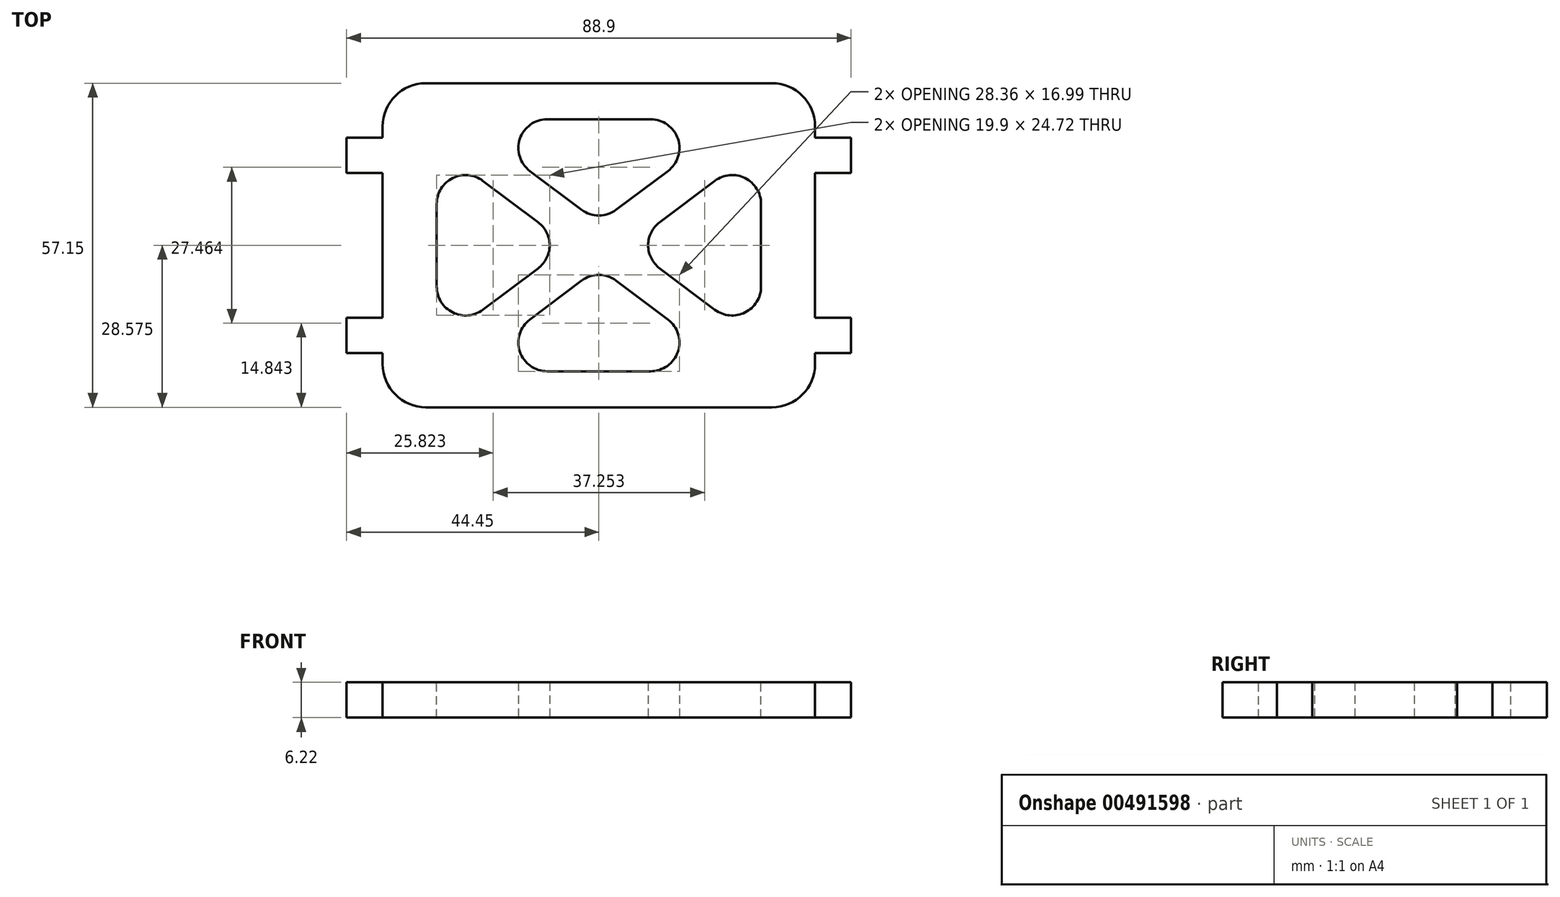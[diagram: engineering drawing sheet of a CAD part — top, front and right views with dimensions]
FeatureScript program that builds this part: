
annotation { "Feature Type Name" : "Feature", "Feature Type Description" : "" }
export const myFeature = defineFeature(function(context is Context, id is Id, definition is map)
    precondition{}
    {
        {
            var Q0;
            Q0=qCreatedBy(makeId("Top.planeOp"),FACE);
            var sketch = newSketch(context, id + "F0", { "sketchPlane" : qUnion([Q0])});
            skLineSegment(sketch, "E0", {"start": v(0, 0) * mm, "end": v(38.1, 0) * mm});
            skLineSegment(sketch, "E1", {"start": v(38.1, 57.15) * mm, "end": v(0, 57.15) * mm});
            skLineSegment(sketch, "E2", {"start": v(1.81, 12.7) * mm, "end": v(54.74, 12.7) * mm, "construction": true});
            skLineSegment(sketch, "E3", {"start": v(1.81, 44.45) * mm, "end": v(54.74, 44.45) * mm, "construction": true});
            skLineSegment(sketch, "E4", {"start": v(44.45, 44.45) * mm, "end": v(44.45, 47.56) * mm});
            skLineSegment(sketch, "E5", {"start": v(44.45, 47.56) * mm, "end": v(38.1, 47.56) * mm});
            skLineSegment(sketch, "E6", {"start": v(44.45, 44.45) * mm, "end": v(44.45, 41.34) * mm});
            skLineSegment(sketch, "E7", {"start": v(44.45, 41.34) * mm, "end": v(38.1, 41.34) * mm});
            skLineSegment(sketch, "E8", {"start": v(44.45, 12.7) * mm, "end": v(44.45, 15.81) * mm});
            skLineSegment(sketch, "E9", {"start": v(44.45, 15.81) * mm, "end": v(38.1, 15.81) * mm});
            skLineSegment(sketch, "E10", {"start": v(44.45, 12.7) * mm, "end": v(44.45, 9.59) * mm});
            skLineSegment(sketch, "E11", {"start": v(44.45, 9.59) * mm, "end": v(38.1, 9.59) * mm});
            skLineSegment(sketch, "E12", {"start": v(38.1, 9.59) * mm, "end": v(38.1, 0) * mm});
            skLineSegment(sketch, "E13", {"start": v(38.1, 15.81) * mm, "end": v(38.1, 41.34) * mm});
            skLineSegment(sketch, "E14", {"start": v(38.1, 47.56) * mm, "end": v(38.1, 57.15) * mm});
            skLineSegment(sketch, "E15.MirrorCS", {"start": v(-38.1, 57.15) * mm, "end": v(0, 57.15) * mm});
            skLineSegment(sketch, "E16.MirrorCS", {"start": v(-38.1, 47.56) * mm, "end": v(-38.1, 57.15) * mm});
            skLineSegment(sketch, "E17.MirrorCS", {"start": v(-44.45, 47.56) * mm, "end": v(-38.1, 47.56) * mm});
            skLineSegment(sketch, "E18.MirrorCS", {"start": v(-44.45, 44.45) * mm, "end": v(-44.45, 47.56) * mm});
            skLineSegment(sketch, "E19.MirrorCS", {"start": v(-44.45, 44.45) * mm, "end": v(-44.45, 41.34) * mm});
            skLineSegment(sketch, "E20.MirrorCS", {"start": v(-44.45, 41.34) * mm, "end": v(-38.1, 41.34) * mm});
            skLineSegment(sketch, "E21.MirrorCS", {"start": v(-38.1, 15.81) * mm, "end": v(-38.1, 41.34) * mm});
            skLineSegment(sketch, "E22.MirrorCS", {"start": v(-44.45, 15.81) * mm, "end": v(-38.1, 15.81) * mm});
            skLineSegment(sketch, "E23.MirrorCS", {"start": v(-44.45, 12.7) * mm, "end": v(-44.45, 15.81) * mm});
            skLineSegment(sketch, "E24.MirrorCS", {"start": v(-44.45, 12.7) * mm, "end": v(-44.45, 9.59) * mm});
            skLineSegment(sketch, "E25.MirrorCS", {"start": v(-44.45, 9.59) * mm, "end": v(-38.1, 9.59) * mm});
            skLineSegment(sketch, "E26.MirrorCS", {"start": v(-38.1, 9.59) * mm, "end": v(-38.1, 0) * mm});
            skLineSegment(sketch, "E27.MirrorCS", {"start": v(0, 0) * mm, "end": v(-38.1, 0) * mm});
            skSolve(sketch);
        }
        {
            var Q0;
            Q0 = qSketchRegion(id + "F0", true);
            extrude(context, id + "F1", {"entities" : qUnion([Q0]), "depth" : 6.22 * mm});
        }
        {
            var Q0;
            Q0=makeQuery(id+"F1.opExtrude","CAP_FACE",FACE,{"disambiguationData":[OSD([sQuery(id+"F0.wireOp",EDGE,"E0"),sQuery(id+"F0.wireOp",EDGE,"E1"),sQuery(id+"F0.wireOp",EDGE,"E4"),sQuery(id+"F0.wireOp",EDGE,"E5"),sQuery(id+"F0.wireOp",EDGE,"E6"),sQuery(id+"F0.wireOp",EDGE,"E7"),sQuery(id+"F0.wireOp",EDGE,"E8"),sQuery(id+"F0.wireOp",EDGE,"E9"),sQuery(id+"F0.wireOp",EDGE,"E10"),sQuery(id+"F0.wireOp",EDGE,"E11"),sQuery(id+"F0.wireOp",EDGE,"E12"),sQuery(id+"F0.wireOp",EDGE,"E13"),sQuery(id+"F0.wireOp",EDGE,"E14"),sQuery(id+"F0.wireOp",EDGE,"E15.MirrorCS"),sQuery(id+"F0.wireOp",EDGE,"E16.MirrorCS"),sQuery(id+"F0.wireOp",EDGE,"E17.MirrorCS"),sQuery(id+"F0.wireOp",EDGE,"E18.MirrorCS"),sQuery(id+"F0.wireOp",EDGE,"E19.MirrorCS"),sQuery(id+"F0.wireOp",EDGE,"E20.MirrorCS"),sQuery(id+"F0.wireOp",EDGE,"E21.MirrorCS"),sQuery(id+"F0.wireOp",EDGE,"E22.MirrorCS"),sQuery(id+"F0.wireOp",EDGE,"E23.MirrorCS"),sQuery(id+"F0.wireOp",EDGE,"E24.MirrorCS"),sQuery(id+"F0.wireOp",EDGE,"E25.MirrorCS"),sQuery(id+"F0.wireOp",EDGE,"E26.MirrorCS"),sQuery(id+"F0.wireOp",EDGE,"E27.MirrorCS")])],"isStart":false});
            var sketch = newSketch(context, id + "F2", { "sketchPlane" : qUnion([Q0])});
            skLineSegment(sketch, "E28", {"start": v(-38.1, 57.15) * mm, "end": v(38.1, 0) * mm, "construction": true});
            skLineSegment(sketch, "E29", {"start": v(38.1, 57.15) * mm, "end": v(-38.1, 0) * mm, "construction": true});
            skLineSegment(sketch, "E30", {"start": v(-31.75, -5.46) * mm, "end": v(-31.75, 61.03) * mm, "construction": true});
            skLineSegment(sketch, "E31", {"start": v(31.75, -6.6) * mm, "end": v(31.75, 61.6) * mm, "construction": true});
            skLineSegment(sketch, "E32", {"start": v(-44.69, 50.8) * mm, "end": v(46.98, 50.8) * mm, "construction": true});
            skLineSegment(sketch, "E33", {"start": v(-48, 6.35) * mm, "end": v(45.68, 6.35) * mm, "construction": true});
            skLineSegment(sketch, "E34", {"start": v(-28.57, 11.11) * mm, "end": v(-5.3, 28.58) * mm});
            skLineSegment(sketch, "E35", {"start": v(-5.3, 28.58) * mm, "end": v(-28.58, 46.04) * mm});
            skLineSegment(sketch, "E36", {"start": v(0, 32.54) * mm, "end": v(-24.34, 50.8) * mm});
            skLineSegment(sketch, "E37", {"start": v(-24.34, 50.8) * mm, "end": v(24.34, 50.8) * mm});
            skLineSegment(sketch, "E38", {"start": v(24.34, 50.8) * mm, "end": v(0, 32.54) * mm});
            skLineSegment(sketch, "E39", {"start": v(-28.58, 46.04) * mm, "end": v(-28.57, 11.11) * mm});
            skLineSegment(sketch, "E40.MirrorCS", {"start": v(5.3, 28.58) * mm, "end": v(28.58, 46.04) * mm});
            skLineSegment(sketch, "E41.MirrorCS", {"start": v(28.58, 46.04) * mm, "end": v(28.57, 11.11) * mm});
            skLineSegment(sketch, "E42.MirrorCS", {"start": v(28.57, 11.11) * mm, "end": v(5.3, 28.58) * mm});
            skLineSegment(sketch, "E43", {"start": v(-46.54, 28.57) * mm, "end": v(53.85, 28.57) * mm, "construction": true});
            skPoint(sketch, "E43.startSnap0", {"position": v(-38.1, 28.57) * mm});
            skLineSegment(sketch, "E44.MirrorCS", {"start": v(0, 24.6) * mm, "end": v(-24.34, 6.35) * mm});
            skLineSegment(sketch, "E45.MirrorCS", {"start": v(24.34, 6.35) * mm, "end": v(0, 24.6) * mm});
            skLineSegment(sketch, "E46.MirrorCS", {"start": v(-24.34, 6.35) * mm, "end": v(24.34, 6.35) * mm});
            skSolve(sketch);
        }
        {
            var Q0;
            Q0 = qSketchRegion(id + "F2", true);
            extrude(context, id + "F3", {"entities" : qUnion([Q0]), "operationType" : NewBodyOperationType.REMOVE, "oppositeDirection" : true, "depth" : 25.4 * mm});
        }
        {
            var Q0;
            Q0=makeQuery(id+"F3.boolean.opBoolean","COPY",EDGE,{"derivedFrom":makeQuery(id+"F3.opExtrude","SWEPT_EDGE",EDGE,{"disambiguationData":[OSD([sQuery(id+"F2.wireOp",EDGE,"E34"),sQuery(id+"F2.wireOp",EDGE,"E39")])]})});
            var Q1;
            Q1=makeQuery(id+"F3.boolean.opBoolean","COPY",EDGE,{"derivedFrom":makeQuery(id+"F3.opExtrude","SWEPT_EDGE",EDGE,{"disambiguationData":[OSD([sQuery(id+"F2.wireOp",EDGE,"E35"),sQuery(id+"F2.wireOp",EDGE,"E39")])]})});
            var Q2;
            Q2=makeQuery(id+"F3.boolean.opBoolean","COPY",EDGE,{"derivedFrom":makeQuery(id+"F3.opExtrude","SWEPT_EDGE",EDGE,{"disambiguationData":[OSD([sQuery(id+"F2.wireOp",EDGE,"E34"),sQuery(id+"F2.wireOp",EDGE,"E35")])]})});
            var Q3;
            Q3=makeQuery(id+"F3.boolean.opBoolean","COPY",EDGE,{"derivedFrom":makeQuery(id+"F3.opExtrude","SWEPT_EDGE",EDGE,{"disambiguationData":[OSD([sQuery(id+"F2.wireOp",EDGE,"E45.MirrorCS"),sQuery(id+"F2.wireOp",EDGE,"E46.MirrorCS")])]})});
            var Q4;
            Q4=makeQuery(id+"F3.boolean.opBoolean","COPY",EDGE,{"derivedFrom":makeQuery(id+"F3.opExtrude","SWEPT_EDGE",EDGE,{"disambiguationData":[OSD([sQuery(id+"F2.wireOp",EDGE,"E44.MirrorCS"),sQuery(id+"F2.wireOp",EDGE,"E45.MirrorCS")])]})});
            var Q5;
            Q5=makeQuery(id+"F3.boolean.opBoolean","COPY",EDGE,{"derivedFrom":makeQuery(id+"F3.opExtrude","SWEPT_EDGE",EDGE,{"disambiguationData":[OSD([sQuery(id+"F2.wireOp",EDGE,"E44.MirrorCS"),sQuery(id+"F2.wireOp",EDGE,"E46.MirrorCS")])]})});
            var Q6;
            Q6=makeQuery(id+"F3.boolean.opBoolean","COPY",EDGE,{"derivedFrom":makeQuery(id+"F3.opExtrude","SWEPT_EDGE",EDGE,{"disambiguationData":[OSD([sQuery(id+"F2.wireOp",EDGE,"E41.MirrorCS"),sQuery(id+"F2.wireOp",EDGE,"E42.MirrorCS")])]})});
            var Q7;
            Q7=makeQuery(id+"F3.boolean.opBoolean","COPY",EDGE,{"derivedFrom":makeQuery(id+"F3.opExtrude","SWEPT_EDGE",EDGE,{"disambiguationData":[OSD([sQuery(id+"F2.wireOp",EDGE,"E40.MirrorCS"),sQuery(id+"F2.wireOp",EDGE,"E41.MirrorCS")])]})});
            var Q8;
            Q8=makeQuery(id+"F3.boolean.opBoolean","COPY",EDGE,{"derivedFrom":makeQuery(id+"F3.opExtrude","SWEPT_EDGE",EDGE,{"disambiguationData":[OSD([sQuery(id+"F2.wireOp",EDGE,"E40.MirrorCS"),sQuery(id+"F2.wireOp",EDGE,"E42.MirrorCS")])]})});
            var Q9;
            Q9=makeQuery(id+"F3.boolean.opBoolean","COPY",EDGE,{"derivedFrom":makeQuery(id+"F3.opExtrude","SWEPT_EDGE",EDGE,{"disambiguationData":[OSD([sQuery(id+"F2.wireOp",EDGE,"E36"),sQuery(id+"F2.wireOp",EDGE,"E38")])]})});
            var Q10;
            Q10=makeQuery(id+"F3.boolean.opBoolean","COPY",EDGE,{"derivedFrom":makeQuery(id+"F3.opExtrude","SWEPT_EDGE",EDGE,{"disambiguationData":[OSD([sQuery(id+"F2.wireOp",EDGE,"E37"),sQuery(id+"F2.wireOp",EDGE,"E38")])]})});
            var Q11;
            Q11=makeQuery(id+"F3.boolean.opBoolean","COPY",EDGE,{"derivedFrom":makeQuery(id+"F3.opExtrude","SWEPT_EDGE",EDGE,{"disambiguationData":[OSD([sQuery(id+"F2.wireOp",EDGE,"E36"),sQuery(id+"F2.wireOp",EDGE,"E37")])]})});
            fillet(context, id + "F4", {"entities" : qUnion([Q0, Q1, Q2, Q3, Q4, Q5, Q6, Q7, Q8, Q9, Q10, Q11]), "radius" : 5.08 * mm, "tangentPropagation" : true, "allowEdgeOverflow" : false});
        }
        {
            var Q0;
            Q0=makeQuery(id+"F1.opExtrude","SWEPT_EDGE",EDGE,{"disambiguationData":[OSD([sQuery(id+"F0.wireOp",EDGE,"E15.MirrorCS"),sQuery(id+"F0.wireOp",EDGE,"E16.MirrorCS")])]});
            var Q1;
            Q1=makeQuery(id+"F1.opExtrude","SWEPT_EDGE",EDGE,{"disambiguationData":[OSD([sQuery(id+"F0.wireOp",EDGE,"E1"),sQuery(id+"F0.wireOp",EDGE,"E14")])]});
            var Q2;
            Q2=makeQuery(id+"F1.opExtrude","SWEPT_EDGE",EDGE,{"disambiguationData":[OSD([sQuery(id+"F0.wireOp",EDGE,"E0"),sQuery(id+"F0.wireOp",EDGE,"E12")])]});
            var Q3;
            Q3=makeQuery(id+"F1.opExtrude","SWEPT_EDGE",EDGE,{"disambiguationData":[OSD([sQuery(id+"F0.wireOp",EDGE,"E26.MirrorCS"),sQuery(id+"F0.wireOp",EDGE,"E27.MirrorCS")])]});
            fillet(context, id + "F5", {"entities" : qUnion([Q0, Q1, Q2, Q3]), "radius" : 7.62 * mm, "tangentPropagation" : true, "allowEdgeOverflow" : false});
        }
    });
